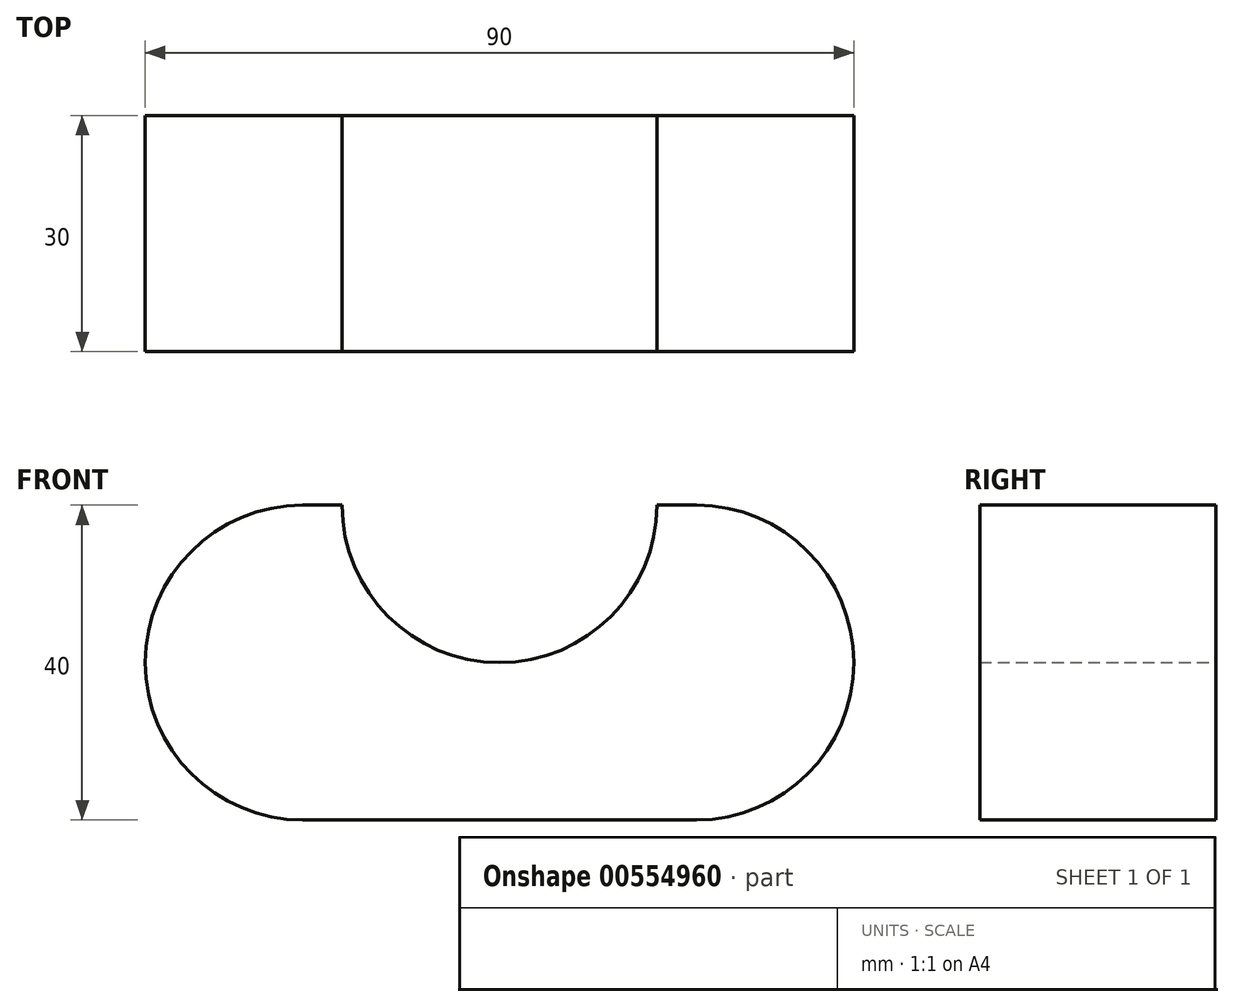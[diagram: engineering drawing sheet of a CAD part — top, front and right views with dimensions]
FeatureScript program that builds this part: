
annotation { "Feature Type Name" : "Feature", "Feature Type Description" : "" }
export const myFeature = defineFeature(function(context is Context, id is Id, definition is map)
    precondition{}
    {
        {
            var Q0;
            Q0=qCreatedBy(makeId("Front.planeOp"),FACE);
            var sketch = newSketch(context, id + "F0", { "sketchPlane" : qUnion([Q0])});
            skLineSegment(sketch, "E0", {"start": v(0, 0) * mm, "end": v(50, 0) * mm});
            skLineSegment(sketch, "E1", {"start": v(50, 40) * mm, "end": v(45, 40) * mm});
            skLineSegment(sketch, "E2", {"start": v(0, 40) * mm, "end": v(5, 40) * mm});
            skArc(sketch, "E3", {"start": v(50, 0) * mm, "mid": v(70, 20) * mm, "end": v(50, 40) * mm});
            skArc(sketch, "E4", {"start": v(0, 40) * mm, "mid": v(-20, 20) * mm, "end": v(0, 0) * mm});
            skArc(sketch, "E5", {"start": v(5, 40) * mm, "mid": v(25, 20) * mm, "end": v(45, 40) * mm});
            skSolve(sketch);
        }
        {
            var Q0;
            Q0 = qSketchRegion(id + "F0", true);
            extrude(context, id + "F1", {"entities" : qUnion([Q0]), "depth" : 30 * mm, "offsetDistance" : 25 * mm});
        }
    });
